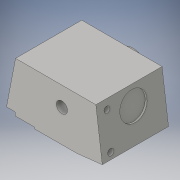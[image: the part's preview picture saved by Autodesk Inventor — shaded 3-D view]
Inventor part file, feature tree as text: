
AUTODESK INVENTOR PART (.ipt)
format: ipt  version: 2016 (Build 200138000, 138)  size: 213,504 bytes
history: native  units: in
note: dims shown in document units (in); Inventor stores cm internally (conversion verified against a paired STEP export)
features: extrude x6, sketch x6, fillet x2
ambient origin geometry x8: Origin, YZ Plane, XZ Plane, XY Plane, X Axis, Y Axis, Z Axis, Center Point
bodies: Solid1 (feature_tree)
feature tree (14):
  extrude  "Extrusion1"  Depth=10.4921in
  sketch  "Sketch3"  dims[d7=10.0in d8=0.5669in]
  extrude  "Extrusion2"  Depth=0.5669in
  extrude  "Extrusion3"  Depth=0.694in
  extrude  "Extrusion4"  Depth=0.7087in
  extrude  "Extrusion5"  Depth=0.0787in
  extrude  "Extrusion6"  Depth=13.4646in TaperAngle=0.0deg
  fillet  "Fillet1"  Radius=5.5118in
  fillet  "Fillet2"  Radius=6.2992in
  sketch  "Sketch1"  dims[d0=8.6614in d1=10.4921in]
  sketch  "Sketch4"  dims[d9=9.6457in d10=0.694in]
  sketch  "Sketch5"  dims[d11=1.7717in d12=0.7087in]
  sketch  "Sketch6"  dims[d14=16.3386in d15=0.0787in]
  sketch  "Sketch7"  dims[d16=0.0787in d17=13.4646in d18=0.0in d22=5.5118in d26=6.2992in d27=2.7559in d28=3.6024in d29=2.7559in d30=0.3937in d31=0.0in d34=1.1811in d37=1.7717in d38=2.0079in d39=1.2402in d42=1.2106in d43=1.8799in d44=2.3622in d45=0.0in d49=6.3386in d50=0.748in d52=7.4213in d53=1.0236in d54=0.0in d55=2.2835in d56=1.0236in d57=0.0in d69=0.7874in d70=1.378in d72=0.3937in d73=0.315in d75=0.2362in d76=0.0in d77=0.0787in d78=0.0787in]
